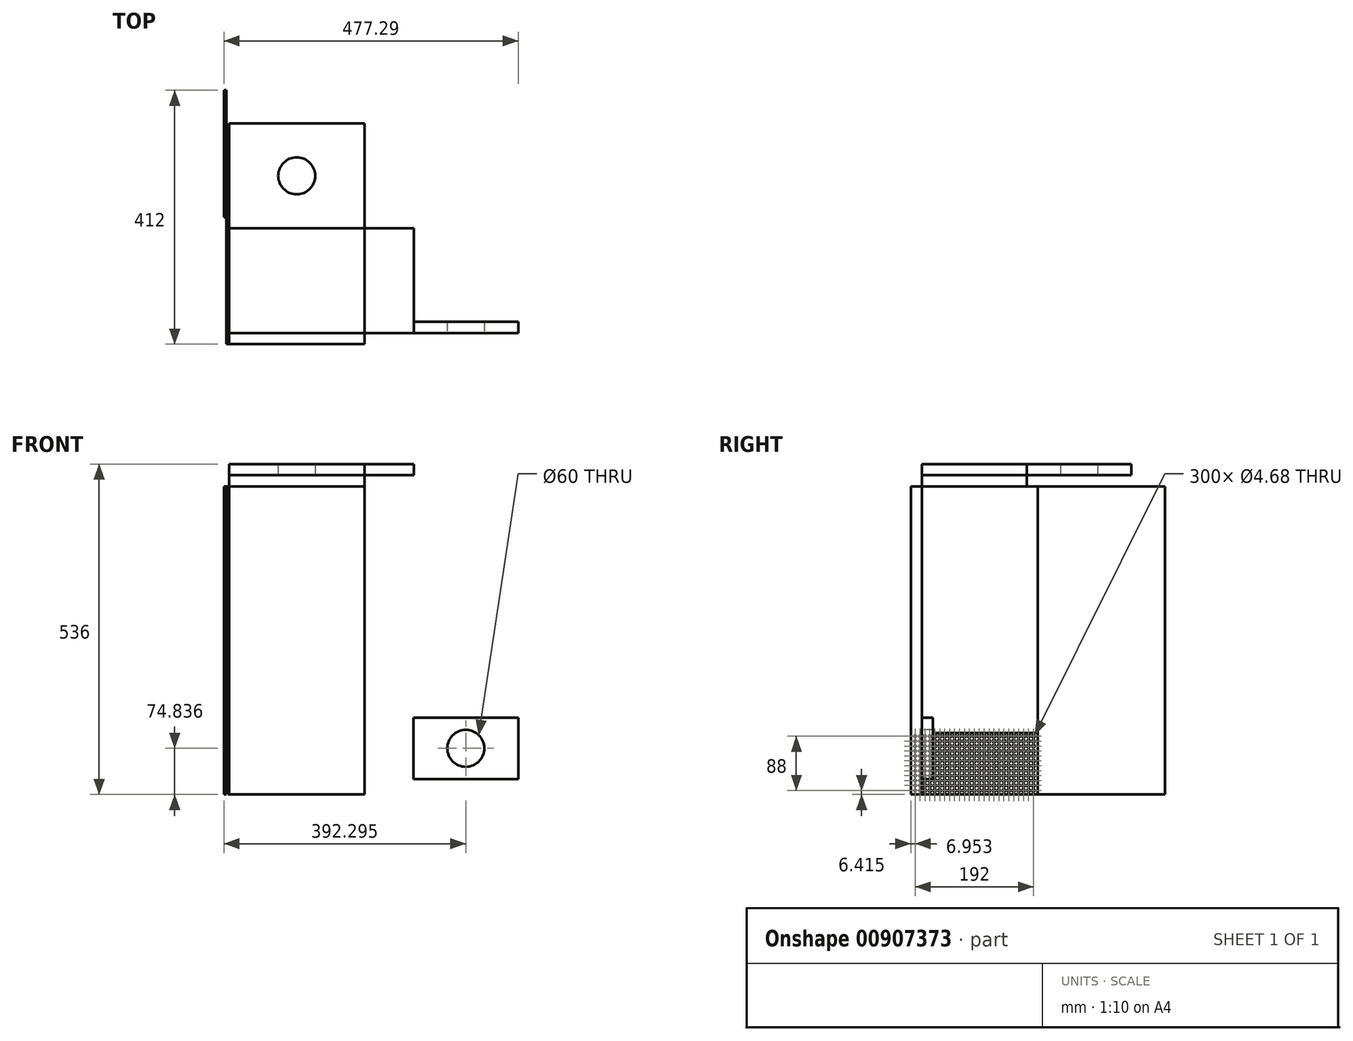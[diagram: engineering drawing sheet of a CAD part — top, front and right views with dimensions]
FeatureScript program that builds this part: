
annotation { "Feature Type Name" : "Feature", "Feature Type Description" : "" }
export const myFeature = defineFeature(function(context is Context, id is Id, definition is map)
    precondition{}
    {
        {
            var Q0;
            Q0=qCreatedBy(makeId("Front.planeOp"),FACE);
            var sketch = newSketch(context, id + "F0", { "sketchPlane" : qUnion([Q0])});
            skLineSegment(sketch, "E0.bottom", {"start": v(-107.52, 319.28) * mm, "end": v(112.48, 319.28) * mm});
            skLineSegment(sketch, "E0.top", {"start": v(-107.52, -180.72) * mm, "end": v(112.48, -180.72) * mm});
            skLineSegment(sketch, "E0.left", {"start": v(-107.52, 319.28) * mm, "end": v(-107.52, -180.72) * mm});
            skLineSegment(sketch, "E0.right", {"start": v(112.48, 319.28) * mm, "end": v(112.48, -180.72) * mm});
            skSolve(sketch);
        }
        {
            var Q0;
            Q0=makeQuery(id+"F0.imprint","IMPRINT",FACE,{"disambiguationData":[TD([[makeQuery(id+"F0.imprint","IMPRINT",EDGE,{"derivedFrom":sQuery(id+"F0.wireOp",EDGE,"E0.bottom")}),-1.0]])]});
            extrude(context, id + "F1", {"entities" : qUnion([Q0]), "depth" : 18 * mm, "offsetDistance" : 25 * mm});
        }
        {
            var Q0;
            Q0=makeQuery(id+"F1.opExtrude","SWEPT_FACE",FACE,{"disambiguationData":[OSD([sQuery(id+"F0.wireOp",EDGE,"E0.bottom")])]});
            var sketch = newSketch(context, id + "F2", { "sketchPlane" : qUnion([Q0])});
            skLineSegment(sketch, "E1.bottom", {"start": v(-107.52, 0) * mm, "end": v(112.48, 0) * mm});
            skLineSegment(sketch, "E1.top", {"start": v(-107.52, 170) * mm, "end": v(112.48, 170) * mm});
            skLineSegment(sketch, "E1.left", {"start": v(-107.52, 0) * mm, "end": v(-107.52, 170) * mm});
            skLineSegment(sketch, "E1.right", {"start": v(112.48, 0) * mm, "end": v(112.48, 170) * mm});
            skSolve(sketch);
        }
        {
            var Q0;
            Q0 = qSketchRegion(id + "F2", true);
            extrude(context, id + "F3", {"entities" : qUnion([Q0]), "depth" : 18 * mm, "offsetDistance" : 25 * mm});
        }
        {
            var Q0;
            Q0=makeQuery(id+"F3.opExtrude","CAP_FACE",FACE,{"disambiguationData":[OSD([sQuery(id+"F2.wireOp",EDGE,"E1.bottom"),sQuery(id+"F2.wireOp",EDGE,"E1.top"),sQuery(id+"F2.wireOp",EDGE,"E1.left"),sQuery(id+"F2.wireOp",EDGE,"E1.right")])],"isStart":false});
            var sketch = newSketch(context, id + "F4", { "sketchPlane" : qUnion([Q0])});
            skLineSegment(sketch, "E2.bottom", {"start": v(-107.52, 170) * mm, "end": v(112.48, 170) * mm});
            skLineSegment(sketch, "E2.top", {"start": v(-107.52, 340) * mm, "end": v(112.48, 340) * mm});
            skLineSegment(sketch, "E2.left", {"start": v(-107.52, 170) * mm, "end": v(-107.52, 340) * mm});
            skLineSegment(sketch, "E2.right", {"start": v(112.48, 170) * mm, "end": v(112.48, 340) * mm});
            skCircle(sketch, "E3", {"center": v(2.48, 255) * mm, "radius": 30 * mm});
            skPoint(sketch, "E3.centerSnap0", {"position": v(112.48, 255) * mm});
            skPoint(sketch, "E3.centerSnap1", {"position": v(2.48, 340) * mm});
            skSolve(sketch);
        }
        {
            var Q0;
            Q0 = qSketchRegion(id + "F4", true);
            extrude(context, id + "F5", {"entities" : qUnion([Q0]), "depth" : 18 * mm, "offsetDistance" : 25 * mm});
        }
        {
            var Q0;
            Q0=makeQuery(id+"F1.opExtrude","SWEPT_FACE",FACE,{"disambiguationData":[OSD([sQuery(id+"F0.wireOp",EDGE,"E0.left")])]});
            var sketch = newSketch(context, id + "F6", { "sketchPlane" : qUnion([Q0])});
            skLineSegment(sketch, "E4.bottom", {"start": v(18, 319.28) * mm, "end": v(-188, 319.28) * mm});
            skLineSegment(sketch, "E4.top", {"start": v(18, -80.72) * mm, "end": v(-188, -80.72) * mm});
            skLineSegment(sketch, "E4.left", {"start": v(18, 319.28) * mm, "end": v(18, -80.72) * mm});
            skLineSegment(sketch, "E4.right", {"start": v(-188, 319.28) * mm, "end": v(-188, -80.72) * mm});
            skSolve(sketch);
        }
        {
            var Q0;
            Q0 = qSketchRegion(id + "F6", true);
            extrude(context, id + "F7", {"entities" : qUnion([Q0]), "depth" : 4 * mm, "offsetDistance" : 25 * mm});
        }
        {
            var Q0;
            Q0=makeQuery(id+"F1.opExtrude","SWEPT_FACE",FACE,{"disambiguationData":[OSD([sQuery(id+"F0.wireOp",EDGE,"E0.left")])]});
            var sketch = newSketch(context, id + "F8", { "sketchPlane" : qUnion([Q0])});
            skLineSegment(sketch, "E5.bottom", {"start": v(18, -180.72) * mm, "end": v(-188, -180.72) * mm});
            skLineSegment(sketch, "E5.top", {"start": v(18, -80.72) * mm, "end": v(-188, -80.72) * mm});
            skLineSegment(sketch, "E5.left", {"start": v(18, -180.72) * mm, "end": v(18, -80.72) * mm});
            skLineSegment(sketch, "E5.right", {"start": v(-188, -180.72) * mm, "end": v(-188, -80.72) * mm});
            skCircle(sketch, "E6", {"center": v(-180.95, -86.3) * mm, "radius": 2.34 * mm});
            skCircle(sketch, "E7.0.1.0", {"center": v(-180.95, -94.3) * mm, "radius": 2.34 * mm});
            skCircle(sketch, "E7.0.2.0", {"center": v(-180.95, -102.3) * mm, "radius": 2.34 * mm});
            skCircle(sketch, "E7.0.3.0", {"center": v(-180.95, -110.3) * mm, "radius": 2.34 * mm});
            skCircle(sketch, "E7.0.4.0", {"center": v(-180.95, -118.3) * mm, "radius": 2.34 * mm});
            skCircle(sketch, "E7.0.5.0", {"center": v(-180.95, -126.3) * mm, "radius": 2.34 * mm});
            skCircle(sketch, "E7.0.6.0", {"center": v(-180.95, -134.3) * mm, "radius": 2.34 * mm});
            skCircle(sketch, "E7.0.7.0", {"center": v(-180.95, -142.3) * mm, "radius": 2.34 * mm});
            skCircle(sketch, "E7.0.8.0", {"center": v(-180.95, -150.3) * mm, "radius": 2.34 * mm});
            skCircle(sketch, "E7.0.9.0", {"center": v(-180.95, -158.3) * mm, "radius": 2.34 * mm});
            skCircle(sketch, "E7.0.10.0", {"center": v(-180.95, -166.3) * mm, "radius": 2.34 * mm});
            skCircle(sketch, "E7.0.11.0", {"center": v(-180.95, -174.3) * mm, "radius": 2.34 * mm});
            skCircle(sketch, "E7.1.0.0", {"center": v(-172.95, -86.3) * mm, "radius": 2.34 * mm});
            skCircle(sketch, "E7.1.1.0", {"center": v(-172.95, -94.3) * mm, "radius": 2.34 * mm});
            skCircle(sketch, "E7.1.2.0", {"center": v(-172.95, -102.3) * mm, "radius": 2.34 * mm});
            skCircle(sketch, "E7.1.3.0", {"center": v(-172.95, -110.3) * mm, "radius": 2.34 * mm});
            skCircle(sketch, "E7.1.4.0", {"center": v(-172.95, -118.3) * mm, "radius": 2.34 * mm});
            skCircle(sketch, "E7.1.5.0", {"center": v(-172.95, -126.3) * mm, "radius": 2.34 * mm});
            skCircle(sketch, "E7.1.6.0", {"center": v(-172.95, -134.3) * mm, "radius": 2.34 * mm});
            skCircle(sketch, "E7.1.7.0", {"center": v(-172.95, -142.3) * mm, "radius": 2.34 * mm});
            skCircle(sketch, "E7.1.8.0", {"center": v(-172.95, -150.3) * mm, "radius": 2.34 * mm});
            skCircle(sketch, "E7.1.9.0", {"center": v(-172.95, -158.3) * mm, "radius": 2.34 * mm});
            skCircle(sketch, "E7.1.10.0", {"center": v(-172.95, -166.3) * mm, "radius": 2.34 * mm});
            skCircle(sketch, "E7.1.11.0", {"center": v(-172.95, -174.3) * mm, "radius": 2.34 * mm});
            skCircle(sketch, "E7.2.0.0", {"center": v(-164.95, -86.3) * mm, "radius": 2.34 * mm});
            skCircle(sketch, "E7.2.1.0", {"center": v(-164.95, -94.3) * mm, "radius": 2.34 * mm});
            skCircle(sketch, "E7.2.2.0", {"center": v(-164.95, -102.3) * mm, "radius": 2.34 * mm});
            skCircle(sketch, "E7.2.3.0", {"center": v(-164.95, -110.3) * mm, "radius": 2.34 * mm});
            skCircle(sketch, "E7.2.4.0", {"center": v(-164.95, -118.3) * mm, "radius": 2.34 * mm});
            skCircle(sketch, "E7.2.5.0", {"center": v(-164.95, -126.3) * mm, "radius": 2.34 * mm});
            skCircle(sketch, "E7.2.6.0", {"center": v(-164.95, -134.3) * mm, "radius": 2.34 * mm});
            skCircle(sketch, "E7.2.7.0", {"center": v(-164.95, -142.3) * mm, "radius": 2.34 * mm});
            skCircle(sketch, "E7.2.8.0", {"center": v(-164.95, -150.3) * mm, "radius": 2.34 * mm});
            skCircle(sketch, "E7.2.9.0", {"center": v(-164.95, -158.3) * mm, "radius": 2.34 * mm});
            skCircle(sketch, "E7.2.10.0", {"center": v(-164.95, -166.3) * mm, "radius": 2.34 * mm});
            skCircle(sketch, "E7.2.11.0", {"center": v(-164.95, -174.3) * mm, "radius": 2.34 * mm});
            skCircle(sketch, "E7.3.0.0", {"center": v(-156.95, -86.3) * mm, "radius": 2.34 * mm});
            skCircle(sketch, "E7.3.1.0", {"center": v(-156.95, -94.3) * mm, "radius": 2.34 * mm});
            skCircle(sketch, "E7.3.2.0", {"center": v(-156.95, -102.3) * mm, "radius": 2.34 * mm});
            skCircle(sketch, "E7.3.3.0", {"center": v(-156.95, -110.3) * mm, "radius": 2.34 * mm});
            skCircle(sketch, "E7.3.4.0", {"center": v(-156.95, -118.3) * mm, "radius": 2.34 * mm});
            skCircle(sketch, "E7.3.5.0", {"center": v(-156.95, -126.3) * mm, "radius": 2.34 * mm});
            skCircle(sketch, "E7.3.6.0", {"center": v(-156.95, -134.3) * mm, "radius": 2.34 * mm});
            skCircle(sketch, "E7.3.7.0", {"center": v(-156.95, -142.3) * mm, "radius": 2.34 * mm});
            skCircle(sketch, "E7.3.8.0", {"center": v(-156.95, -150.3) * mm, "radius": 2.34 * mm});
            skCircle(sketch, "E7.3.9.0", {"center": v(-156.95, -158.3) * mm, "radius": 2.34 * mm});
            skCircle(sketch, "E7.3.10.0", {"center": v(-156.95, -166.3) * mm, "radius": 2.34 * mm});
            skCircle(sketch, "E7.3.11.0", {"center": v(-156.95, -174.3) * mm, "radius": 2.34 * mm});
            skCircle(sketch, "E7.4.0.0", {"center": v(-148.95, -86.3) * mm, "radius": 2.34 * mm});
            skCircle(sketch, "E7.4.1.0", {"center": v(-148.95, -94.3) * mm, "radius": 2.34 * mm});
            skCircle(sketch, "E7.4.2.0", {"center": v(-148.95, -102.3) * mm, "radius": 2.34 * mm});
            skCircle(sketch, "E7.4.3.0", {"center": v(-148.95, -110.3) * mm, "radius": 2.34 * mm});
            skCircle(sketch, "E7.4.4.0", {"center": v(-148.95, -118.3) * mm, "radius": 2.34 * mm});
            skCircle(sketch, "E7.4.5.0", {"center": v(-148.95, -126.3) * mm, "radius": 2.34 * mm});
            skCircle(sketch, "E7.4.6.0", {"center": v(-148.95, -134.3) * mm, "radius": 2.34 * mm});
            skCircle(sketch, "E7.4.7.0", {"center": v(-148.95, -142.3) * mm, "radius": 2.34 * mm});
            skCircle(sketch, "E7.4.8.0", {"center": v(-148.95, -150.3) * mm, "radius": 2.34 * mm});
            skCircle(sketch, "E7.4.9.0", {"center": v(-148.95, -158.3) * mm, "radius": 2.34 * mm});
            skCircle(sketch, "E7.4.10.0", {"center": v(-148.95, -166.3) * mm, "radius": 2.34 * mm});
            skCircle(sketch, "E7.4.11.0", {"center": v(-148.95, -174.3) * mm, "radius": 2.34 * mm});
            skCircle(sketch, "E7.5.0.0", {"center": v(-140.95, -86.3) * mm, "radius": 2.34 * mm});
            skCircle(sketch, "E7.5.1.0", {"center": v(-140.95, -94.3) * mm, "radius": 2.34 * mm});
            skCircle(sketch, "E7.5.2.0", {"center": v(-140.95, -102.3) * mm, "radius": 2.34 * mm});
            skCircle(sketch, "E7.5.3.0", {"center": v(-140.95, -110.3) * mm, "radius": 2.34 * mm});
            skCircle(sketch, "E7.5.4.0", {"center": v(-140.95, -118.3) * mm, "radius": 2.34 * mm});
            skCircle(sketch, "E7.5.5.0", {"center": v(-140.95, -126.3) * mm, "radius": 2.34 * mm});
            skCircle(sketch, "E7.5.6.0", {"center": v(-140.95, -134.3) * mm, "radius": 2.34 * mm});
            skCircle(sketch, "E7.5.7.0", {"center": v(-140.95, -142.3) * mm, "radius": 2.34 * mm});
            skCircle(sketch, "E7.5.8.0", {"center": v(-140.95, -150.3) * mm, "radius": 2.34 * mm});
            skCircle(sketch, "E7.5.9.0", {"center": v(-140.95, -158.3) * mm, "radius": 2.34 * mm});
            skCircle(sketch, "E7.5.10.0", {"center": v(-140.95, -166.3) * mm, "radius": 2.34 * mm});
            skCircle(sketch, "E7.5.11.0", {"center": v(-140.95, -174.3) * mm, "radius": 2.34 * mm});
            skCircle(sketch, "E7.6.0.0", {"center": v(-132.95, -86.3) * mm, "radius": 2.34 * mm});
            skCircle(sketch, "E7.6.1.0", {"center": v(-132.95, -94.3) * mm, "radius": 2.34 * mm});
            skCircle(sketch, "E7.6.2.0", {"center": v(-132.95, -102.3) * mm, "radius": 2.34 * mm});
            skCircle(sketch, "E7.6.3.0", {"center": v(-132.95, -110.3) * mm, "radius": 2.34 * mm});
            skCircle(sketch, "E7.6.4.0", {"center": v(-132.95, -118.3) * mm, "radius": 2.34 * mm});
            skCircle(sketch, "E7.6.5.0", {"center": v(-132.95, -126.3) * mm, "radius": 2.34 * mm});
            skCircle(sketch, "E7.6.6.0", {"center": v(-132.95, -134.3) * mm, "radius": 2.34 * mm});
            skCircle(sketch, "E7.6.7.0", {"center": v(-132.95, -142.3) * mm, "radius": 2.34 * mm});
            skCircle(sketch, "E7.6.8.0", {"center": v(-132.95, -150.3) * mm, "radius": 2.34 * mm});
            skCircle(sketch, "E7.6.9.0", {"center": v(-132.95, -158.3) * mm, "radius": 2.34 * mm});
            skCircle(sketch, "E7.6.10.0", {"center": v(-132.95, -166.3) * mm, "radius": 2.34 * mm});
            skCircle(sketch, "E7.6.11.0", {"center": v(-132.95, -174.3) * mm, "radius": 2.34 * mm});
            skCircle(sketch, "E7.7.0.0", {"center": v(-124.95, -86.3) * mm, "radius": 2.34 * mm});
            skCircle(sketch, "E7.7.1.0", {"center": v(-124.95, -94.3) * mm, "radius": 2.34 * mm});
            skCircle(sketch, "E7.7.2.0", {"center": v(-124.95, -102.3) * mm, "radius": 2.34 * mm});
            skCircle(sketch, "E7.7.3.0", {"center": v(-124.95, -110.3) * mm, "radius": 2.34 * mm});
            skCircle(sketch, "E7.7.4.0", {"center": v(-124.95, -118.3) * mm, "radius": 2.34 * mm});
            skCircle(sketch, "E7.7.5.0", {"center": v(-124.95, -126.3) * mm, "radius": 2.34 * mm});
            skCircle(sketch, "E7.7.6.0", {"center": v(-124.95, -134.3) * mm, "radius": 2.34 * mm});
            skCircle(sketch, "E7.7.7.0", {"center": v(-124.95, -142.3) * mm, "radius": 2.34 * mm});
            skCircle(sketch, "E7.7.8.0", {"center": v(-124.95, -150.3) * mm, "radius": 2.34 * mm});
            skCircle(sketch, "E7.7.9.0", {"center": v(-124.95, -158.3) * mm, "radius": 2.34 * mm});
            skCircle(sketch, "E7.7.10.0", {"center": v(-124.95, -166.3) * mm, "radius": 2.34 * mm});
            skCircle(sketch, "E7.7.11.0", {"center": v(-124.95, -174.3) * mm, "radius": 2.34 * mm});
            skCircle(sketch, "E7.8.0.0", {"center": v(-116.95, -86.3) * mm, "radius": 2.34 * mm});
            skCircle(sketch, "E7.8.1.0", {"center": v(-116.95, -94.3) * mm, "radius": 2.34 * mm});
            skCircle(sketch, "E7.8.2.0", {"center": v(-116.95, -102.3) * mm, "radius": 2.34 * mm});
            skCircle(sketch, "E7.8.3.0", {"center": v(-116.95, -110.3) * mm, "radius": 2.34 * mm});
            skCircle(sketch, "E7.8.4.0", {"center": v(-116.95, -118.3) * mm, "radius": 2.34 * mm});
            skCircle(sketch, "E7.8.5.0", {"center": v(-116.95, -126.3) * mm, "radius": 2.34 * mm});
            skCircle(sketch, "E7.8.6.0", {"center": v(-116.95, -134.3) * mm, "radius": 2.34 * mm});
            skCircle(sketch, "E7.8.7.0", {"center": v(-116.95, -142.3) * mm, "radius": 2.34 * mm});
            skCircle(sketch, "E7.8.8.0", {"center": v(-116.95, -150.3) * mm, "radius": 2.34 * mm});
            skCircle(sketch, "E7.8.9.0", {"center": v(-116.95, -158.3) * mm, "radius": 2.34 * mm});
            skCircle(sketch, "E7.8.10.0", {"center": v(-116.95, -166.3) * mm, "radius": 2.34 * mm});
            skCircle(sketch, "E7.8.11.0", {"center": v(-116.95, -174.3) * mm, "radius": 2.34 * mm});
            skCircle(sketch, "E7.9.0.0", {"center": v(-108.95, -86.3) * mm, "radius": 2.34 * mm});
            skCircle(sketch, "E7.9.1.0", {"center": v(-108.95, -94.3) * mm, "radius": 2.34 * mm});
            skCircle(sketch, "E7.9.2.0", {"center": v(-108.95, -102.3) * mm, "radius": 2.34 * mm});
            skCircle(sketch, "E7.9.3.0", {"center": v(-108.95, -110.3) * mm, "radius": 2.34 * mm});
            skCircle(sketch, "E7.9.4.0", {"center": v(-108.95, -118.3) * mm, "radius": 2.34 * mm});
            skCircle(sketch, "E7.9.5.0", {"center": v(-108.95, -126.3) * mm, "radius": 2.34 * mm});
            skCircle(sketch, "E7.9.6.0", {"center": v(-108.95, -134.3) * mm, "radius": 2.34 * mm});
            skCircle(sketch, "E7.9.7.0", {"center": v(-108.95, -142.3) * mm, "radius": 2.34 * mm});
            skCircle(sketch, "E7.9.8.0", {"center": v(-108.95, -150.3) * mm, "radius": 2.34 * mm});
            skCircle(sketch, "E7.9.9.0", {"center": v(-108.95, -158.3) * mm, "radius": 2.34 * mm});
            skCircle(sketch, "E7.9.10.0", {"center": v(-108.95, -166.3) * mm, "radius": 2.34 * mm});
            skCircle(sketch, "E7.9.11.0", {"center": v(-108.95, -174.3) * mm, "radius": 2.34 * mm});
            skCircle(sketch, "E7.10.0.0", {"center": v(-100.95, -86.3) * mm, "radius": 2.34 * mm});
            skCircle(sketch, "E7.10.1.0", {"center": v(-100.95, -94.3) * mm, "radius": 2.34 * mm});
            skCircle(sketch, "E7.10.2.0", {"center": v(-100.95, -102.3) * mm, "radius": 2.34 * mm});
            skCircle(sketch, "E7.10.3.0", {"center": v(-100.95, -110.3) * mm, "radius": 2.34 * mm});
            skCircle(sketch, "E7.10.4.0", {"center": v(-100.95, -118.3) * mm, "radius": 2.34 * mm});
            skCircle(sketch, "E7.10.5.0", {"center": v(-100.95, -126.3) * mm, "radius": 2.34 * mm});
            skCircle(sketch, "E7.10.6.0", {"center": v(-100.95, -134.3) * mm, "radius": 2.34 * mm});
            skCircle(sketch, "E7.10.7.0", {"center": v(-100.95, -142.3) * mm, "radius": 2.34 * mm});
            skCircle(sketch, "E7.10.8.0", {"center": v(-100.95, -150.3) * mm, "radius": 2.34 * mm});
            skCircle(sketch, "E7.10.9.0", {"center": v(-100.95, -158.3) * mm, "radius": 2.34 * mm});
            skCircle(sketch, "E7.10.10.0", {"center": v(-100.95, -166.3) * mm, "radius": 2.34 * mm});
            skCircle(sketch, "E7.10.11.0", {"center": v(-100.95, -174.3) * mm, "radius": 2.34 * mm});
            skCircle(sketch, "E7.11.0.0", {"center": v(-92.95, -86.3) * mm, "radius": 2.34 * mm});
            skCircle(sketch, "E7.11.1.0", {"center": v(-92.95, -94.3) * mm, "radius": 2.34 * mm});
            skCircle(sketch, "E7.11.2.0", {"center": v(-92.95, -102.3) * mm, "radius": 2.34 * mm});
            skCircle(sketch, "E7.11.3.0", {"center": v(-92.95, -110.3) * mm, "radius": 2.34 * mm});
            skCircle(sketch, "E7.11.4.0", {"center": v(-92.95, -118.3) * mm, "radius": 2.34 * mm});
            skCircle(sketch, "E7.11.5.0", {"center": v(-92.95, -126.3) * mm, "radius": 2.34 * mm});
            skCircle(sketch, "E7.11.6.0", {"center": v(-92.95, -134.3) * mm, "radius": 2.34 * mm});
            skCircle(sketch, "E7.11.7.0", {"center": v(-92.95, -142.3) * mm, "radius": 2.34 * mm});
            skCircle(sketch, "E7.11.8.0", {"center": v(-92.95, -150.3) * mm, "radius": 2.34 * mm});
            skCircle(sketch, "E7.11.9.0", {"center": v(-92.95, -158.3) * mm, "radius": 2.34 * mm});
            skCircle(sketch, "E7.11.10.0", {"center": v(-92.95, -166.3) * mm, "radius": 2.34 * mm});
            skCircle(sketch, "E7.11.11.0", {"center": v(-92.95, -174.3) * mm, "radius": 2.34 * mm});
            skCircle(sketch, "E7.12.0.0", {"center": v(-84.95, -86.3) * mm, "radius": 2.34 * mm});
            skCircle(sketch, "E7.12.1.0", {"center": v(-84.95, -94.3) * mm, "radius": 2.34 * mm});
            skCircle(sketch, "E7.12.2.0", {"center": v(-84.95, -102.3) * mm, "radius": 2.34 * mm});
            skCircle(sketch, "E7.12.3.0", {"center": v(-84.95, -110.3) * mm, "radius": 2.34 * mm});
            skCircle(sketch, "E7.12.4.0", {"center": v(-84.95, -118.3) * mm, "radius": 2.34 * mm});
            skCircle(sketch, "E7.12.5.0", {"center": v(-84.95, -126.3) * mm, "radius": 2.34 * mm});
            skCircle(sketch, "E7.12.6.0", {"center": v(-84.95, -134.3) * mm, "radius": 2.34 * mm});
            skCircle(sketch, "E7.12.7.0", {"center": v(-84.95, -142.3) * mm, "radius": 2.34 * mm});
            skCircle(sketch, "E7.12.8.0", {"center": v(-84.95, -150.3) * mm, "radius": 2.34 * mm});
            skCircle(sketch, "E7.12.9.0", {"center": v(-84.95, -158.3) * mm, "radius": 2.34 * mm});
            skCircle(sketch, "E7.12.10.0", {"center": v(-84.95, -166.3) * mm, "radius": 2.34 * mm});
            skCircle(sketch, "E7.12.11.0", {"center": v(-84.95, -174.3) * mm, "radius": 2.34 * mm});
            skCircle(sketch, "E7.13.0.0", {"center": v(-76.95, -86.3) * mm, "radius": 2.34 * mm});
            skCircle(sketch, "E7.13.1.0", {"center": v(-76.95, -94.3) * mm, "radius": 2.34 * mm});
            skCircle(sketch, "E7.13.2.0", {"center": v(-76.95, -102.3) * mm, "radius": 2.34 * mm});
            skCircle(sketch, "E7.13.3.0", {"center": v(-76.95, -110.3) * mm, "radius": 2.34 * mm});
            skCircle(sketch, "E7.13.4.0", {"center": v(-76.95, -118.3) * mm, "radius": 2.34 * mm});
            skCircle(sketch, "E7.13.5.0", {"center": v(-76.95, -126.3) * mm, "radius": 2.34 * mm});
            skCircle(sketch, "E7.13.6.0", {"center": v(-76.95, -134.3) * mm, "radius": 2.34 * mm});
            skCircle(sketch, "E7.13.7.0", {"center": v(-76.95, -142.3) * mm, "radius": 2.34 * mm});
            skCircle(sketch, "E7.13.8.0", {"center": v(-76.95, -150.3) * mm, "radius": 2.34 * mm});
            skCircle(sketch, "E7.13.9.0", {"center": v(-76.95, -158.3) * mm, "radius": 2.34 * mm});
            skCircle(sketch, "E7.13.10.0", {"center": v(-76.95, -166.3) * mm, "radius": 2.34 * mm});
            skCircle(sketch, "E7.13.11.0", {"center": v(-76.95, -174.3) * mm, "radius": 2.34 * mm});
            skCircle(sketch, "E7.14.0.0", {"center": v(-68.95, -86.3) * mm, "radius": 2.34 * mm});
            skCircle(sketch, "E7.14.1.0", {"center": v(-68.95, -94.3) * mm, "radius": 2.34 * mm});
            skCircle(sketch, "E7.14.2.0", {"center": v(-68.95, -102.3) * mm, "radius": 2.34 * mm});
            skCircle(sketch, "E7.14.3.0", {"center": v(-68.95, -110.3) * mm, "radius": 2.34 * mm});
            skCircle(sketch, "E7.14.4.0", {"center": v(-68.95, -118.3) * mm, "radius": 2.34 * mm});
            skCircle(sketch, "E7.14.5.0", {"center": v(-68.95, -126.3) * mm, "radius": 2.34 * mm});
            skCircle(sketch, "E7.14.6.0", {"center": v(-68.95, -134.3) * mm, "radius": 2.34 * mm});
            skCircle(sketch, "E7.14.7.0", {"center": v(-68.95, -142.3) * mm, "radius": 2.34 * mm});
            skCircle(sketch, "E7.14.8.0", {"center": v(-68.95, -150.3) * mm, "radius": 2.34 * mm});
            skCircle(sketch, "E7.14.9.0", {"center": v(-68.95, -158.3) * mm, "radius": 2.34 * mm});
            skCircle(sketch, "E7.14.10.0", {"center": v(-68.95, -166.3) * mm, "radius": 2.34 * mm});
            skCircle(sketch, "E7.14.11.0", {"center": v(-68.95, -174.3) * mm, "radius": 2.34 * mm});
            skCircle(sketch, "E7.15.0.0", {"center": v(-60.95, -86.3) * mm, "radius": 2.34 * mm});
            skCircle(sketch, "E7.15.1.0", {"center": v(-60.95, -94.3) * mm, "radius": 2.34 * mm});
            skCircle(sketch, "E7.15.2.0", {"center": v(-60.95, -102.3) * mm, "radius": 2.34 * mm});
            skCircle(sketch, "E7.15.3.0", {"center": v(-60.95, -110.3) * mm, "radius": 2.34 * mm});
            skCircle(sketch, "E7.15.4.0", {"center": v(-60.95, -118.3) * mm, "radius": 2.34 * mm});
            skCircle(sketch, "E7.15.5.0", {"center": v(-60.95, -126.3) * mm, "radius": 2.34 * mm});
            skCircle(sketch, "E7.15.6.0", {"center": v(-60.95, -134.3) * mm, "radius": 2.34 * mm});
            skCircle(sketch, "E7.15.7.0", {"center": v(-60.95, -142.3) * mm, "radius": 2.34 * mm});
            skCircle(sketch, "E7.15.8.0", {"center": v(-60.95, -150.3) * mm, "radius": 2.34 * mm});
            skCircle(sketch, "E7.15.9.0", {"center": v(-60.95, -158.3) * mm, "radius": 2.34 * mm});
            skCircle(sketch, "E7.15.10.0", {"center": v(-60.95, -166.3) * mm, "radius": 2.34 * mm});
            skCircle(sketch, "E7.15.11.0", {"center": v(-60.95, -174.3) * mm, "radius": 2.34 * mm});
            skCircle(sketch, "E7.16.0.0", {"center": v(-52.95, -86.3) * mm, "radius": 2.34 * mm});
            skCircle(sketch, "E7.16.1.0", {"center": v(-52.95, -94.3) * mm, "radius": 2.34 * mm});
            skCircle(sketch, "E7.16.2.0", {"center": v(-52.95, -102.3) * mm, "radius": 2.34 * mm});
            skCircle(sketch, "E7.16.3.0", {"center": v(-52.95, -110.3) * mm, "radius": 2.34 * mm});
            skCircle(sketch, "E7.16.4.0", {"center": v(-52.95, -118.3) * mm, "radius": 2.34 * mm});
            skCircle(sketch, "E7.16.5.0", {"center": v(-52.95, -126.3) * mm, "radius": 2.34 * mm});
            skCircle(sketch, "E7.16.6.0", {"center": v(-52.95, -134.3) * mm, "radius": 2.34 * mm});
            skCircle(sketch, "E7.16.7.0", {"center": v(-52.95, -142.3) * mm, "radius": 2.34 * mm});
            skCircle(sketch, "E7.16.8.0", {"center": v(-52.95, -150.3) * mm, "radius": 2.34 * mm});
            skCircle(sketch, "E7.16.9.0", {"center": v(-52.95, -158.3) * mm, "radius": 2.34 * mm});
            skCircle(sketch, "E7.16.10.0", {"center": v(-52.95, -166.3) * mm, "radius": 2.34 * mm});
            skCircle(sketch, "E7.16.11.0", {"center": v(-52.95, -174.3) * mm, "radius": 2.34 * mm});
            skCircle(sketch, "E7.17.0.0", {"center": v(-44.95, -86.3) * mm, "radius": 2.34 * mm});
            skCircle(sketch, "E7.17.1.0", {"center": v(-44.95, -94.3) * mm, "radius": 2.34 * mm});
            skCircle(sketch, "E7.17.2.0", {"center": v(-44.95, -102.3) * mm, "radius": 2.34 * mm});
            skCircle(sketch, "E7.17.3.0", {"center": v(-44.95, -110.3) * mm, "radius": 2.34 * mm});
            skCircle(sketch, "E7.17.4.0", {"center": v(-44.95, -118.3) * mm, "radius": 2.34 * mm});
            skCircle(sketch, "E7.17.5.0", {"center": v(-44.95, -126.3) * mm, "radius": 2.34 * mm});
            skCircle(sketch, "E7.17.6.0", {"center": v(-44.95, -134.3) * mm, "radius": 2.34 * mm});
            skCircle(sketch, "E7.17.7.0", {"center": v(-44.95, -142.3) * mm, "radius": 2.34 * mm});
            skCircle(sketch, "E7.17.8.0", {"center": v(-44.95, -150.3) * mm, "radius": 2.34 * mm});
            skCircle(sketch, "E7.17.9.0", {"center": v(-44.95, -158.3) * mm, "radius": 2.34 * mm});
            skCircle(sketch, "E7.17.10.0", {"center": v(-44.95, -166.3) * mm, "radius": 2.34 * mm});
            skCircle(sketch, "E7.17.11.0", {"center": v(-44.95, -174.3) * mm, "radius": 2.34 * mm});
            skCircle(sketch, "E7.18.0.0", {"center": v(-36.95, -86.3) * mm, "radius": 2.34 * mm});
            skCircle(sketch, "E7.18.1.0", {"center": v(-36.95, -94.3) * mm, "radius": 2.34 * mm});
            skCircle(sketch, "E7.18.2.0", {"center": v(-36.95, -102.3) * mm, "radius": 2.34 * mm});
            skCircle(sketch, "E7.18.3.0", {"center": v(-36.95, -110.3) * mm, "radius": 2.34 * mm});
            skCircle(sketch, "E7.18.4.0", {"center": v(-36.95, -118.3) * mm, "radius": 2.34 * mm});
            skCircle(sketch, "E7.18.5.0", {"center": v(-36.95, -126.3) * mm, "radius": 2.34 * mm});
            skCircle(sketch, "E7.18.6.0", {"center": v(-36.95, -134.3) * mm, "radius": 2.34 * mm});
            skCircle(sketch, "E7.18.7.0", {"center": v(-36.95, -142.3) * mm, "radius": 2.34 * mm});
            skCircle(sketch, "E7.18.8.0", {"center": v(-36.95, -150.3) * mm, "radius": 2.34 * mm});
            skCircle(sketch, "E7.18.9.0", {"center": v(-36.95, -158.3) * mm, "radius": 2.34 * mm});
            skCircle(sketch, "E7.18.10.0", {"center": v(-36.95, -166.3) * mm, "radius": 2.34 * mm});
            skCircle(sketch, "E7.18.11.0", {"center": v(-36.95, -174.3) * mm, "radius": 2.34 * mm});
            skCircle(sketch, "E7.19.0.0", {"center": v(-28.95, -86.3) * mm, "radius": 2.34 * mm});
            skCircle(sketch, "E7.19.1.0", {"center": v(-28.95, -94.3) * mm, "radius": 2.34 * mm});
            skCircle(sketch, "E7.19.2.0", {"center": v(-28.95, -102.3) * mm, "radius": 2.34 * mm});
            skCircle(sketch, "E7.19.3.0", {"center": v(-28.95, -110.3) * mm, "radius": 2.34 * mm});
            skCircle(sketch, "E7.19.4.0", {"center": v(-28.95, -118.3) * mm, "radius": 2.34 * mm});
            skCircle(sketch, "E7.19.5.0", {"center": v(-28.95, -126.3) * mm, "radius": 2.34 * mm});
            skCircle(sketch, "E7.19.6.0", {"center": v(-28.95, -134.3) * mm, "radius": 2.34 * mm});
            skCircle(sketch, "E7.19.7.0", {"center": v(-28.95, -142.3) * mm, "radius": 2.34 * mm});
            skCircle(sketch, "E7.19.8.0", {"center": v(-28.95, -150.3) * mm, "radius": 2.34 * mm});
            skCircle(sketch, "E7.19.9.0", {"center": v(-28.95, -158.3) * mm, "radius": 2.34 * mm});
            skCircle(sketch, "E7.19.10.0", {"center": v(-28.95, -166.3) * mm, "radius": 2.34 * mm});
            skCircle(sketch, "E7.19.11.0", {"center": v(-28.95, -174.3) * mm, "radius": 2.34 * mm});
            skCircle(sketch, "E7.20.0.0", {"center": v(-20.95, -86.3) * mm, "radius": 2.34 * mm});
            skCircle(sketch, "E7.20.1.0", {"center": v(-20.95, -94.3) * mm, "radius": 2.34 * mm});
            skCircle(sketch, "E7.20.2.0", {"center": v(-20.95, -102.3) * mm, "radius": 2.34 * mm});
            skCircle(sketch, "E7.20.3.0", {"center": v(-20.95, -110.3) * mm, "radius": 2.34 * mm});
            skCircle(sketch, "E7.20.4.0", {"center": v(-20.95, -118.3) * mm, "radius": 2.34 * mm});
            skCircle(sketch, "E7.20.5.0", {"center": v(-20.95, -126.3) * mm, "radius": 2.34 * mm});
            skCircle(sketch, "E7.20.6.0", {"center": v(-20.95, -134.3) * mm, "radius": 2.34 * mm});
            skCircle(sketch, "E7.20.7.0", {"center": v(-20.95, -142.3) * mm, "radius": 2.34 * mm});
            skCircle(sketch, "E7.20.8.0", {"center": v(-20.95, -150.3) * mm, "radius": 2.34 * mm});
            skCircle(sketch, "E7.20.9.0", {"center": v(-20.95, -158.3) * mm, "radius": 2.34 * mm});
            skCircle(sketch, "E7.20.10.0", {"center": v(-20.95, -166.3) * mm, "radius": 2.34 * mm});
            skCircle(sketch, "E7.20.11.0", {"center": v(-20.95, -174.3) * mm, "radius": 2.34 * mm});
            skCircle(sketch, "E7.21.0.0", {"center": v(-12.95, -86.3) * mm, "radius": 2.34 * mm});
            skCircle(sketch, "E7.21.1.0", {"center": v(-12.95, -94.3) * mm, "radius": 2.34 * mm});
            skCircle(sketch, "E7.21.2.0", {"center": v(-12.95, -102.3) * mm, "radius": 2.34 * mm});
            skCircle(sketch, "E7.21.3.0", {"center": v(-12.95, -110.3) * mm, "radius": 2.34 * mm});
            skCircle(sketch, "E7.21.4.0", {"center": v(-12.95, -118.3) * mm, "radius": 2.34 * mm});
            skCircle(sketch, "E7.21.5.0", {"center": v(-12.95, -126.3) * mm, "radius": 2.34 * mm});
            skCircle(sketch, "E7.21.6.0", {"center": v(-12.95, -134.3) * mm, "radius": 2.34 * mm});
            skCircle(sketch, "E7.21.7.0", {"center": v(-12.95, -142.3) * mm, "radius": 2.34 * mm});
            skCircle(sketch, "E7.21.8.0", {"center": v(-12.95, -150.3) * mm, "radius": 2.34 * mm});
            skCircle(sketch, "E7.21.9.0", {"center": v(-12.95, -158.3) * mm, "radius": 2.34 * mm});
            skCircle(sketch, "E7.21.10.0", {"center": v(-12.95, -166.3) * mm, "radius": 2.34 * mm});
            skCircle(sketch, "E7.21.11.0", {"center": v(-12.95, -174.3) * mm, "radius": 2.34 * mm});
            skCircle(sketch, "E7.22.0.0", {"center": v(-4.95, -86.3) * mm, "radius": 2.34 * mm});
            skCircle(sketch, "E7.22.1.0", {"center": v(-4.95, -94.3) * mm, "radius": 2.34 * mm});
            skCircle(sketch, "E7.22.2.0", {"center": v(-4.95, -102.3) * mm, "radius": 2.34 * mm});
            skCircle(sketch, "E7.22.3.0", {"center": v(-4.95, -110.3) * mm, "radius": 2.34 * mm});
            skCircle(sketch, "E7.22.4.0", {"center": v(-4.95, -118.3) * mm, "radius": 2.34 * mm});
            skCircle(sketch, "E7.22.5.0", {"center": v(-4.95, -126.3) * mm, "radius": 2.34 * mm});
            skCircle(sketch, "E7.22.6.0", {"center": v(-4.95, -134.3) * mm, "radius": 2.34 * mm});
            skCircle(sketch, "E7.22.7.0", {"center": v(-4.95, -142.3) * mm, "radius": 2.34 * mm});
            skCircle(sketch, "E7.22.8.0", {"center": v(-4.95, -150.3) * mm, "radius": 2.34 * mm});
            skCircle(sketch, "E7.22.9.0", {"center": v(-4.95, -158.3) * mm, "radius": 2.34 * mm});
            skCircle(sketch, "E7.22.10.0", {"center": v(-4.95, -166.3) * mm, "radius": 2.34 * mm});
            skCircle(sketch, "E7.22.11.0", {"center": v(-4.95, -174.3) * mm, "radius": 2.34 * mm});
            skLineSegment(sketch, "E7.direction1", {"start": v(-180.95, -86.3) * mm, "end": v(-172.95, -86.3) * mm, "construction": true});
            skLineSegment(sketch, "E7.direction2", {"start": v(-180.95, -86.3) * mm, "end": v(-180.95, -94.3) * mm, "construction": true});
            skCircle(sketch, "E8.0.23.0", {"center": v(3.05, -86.3) * mm, "radius": 2.34 * mm});
            skCircle(sketch, "E8.0.23.1", {"center": v(3.05, -94.3) * mm, "radius": 2.34 * mm});
            skCircle(sketch, "E8.0.23.2", {"center": v(3.05, -102.3) * mm, "radius": 2.34 * mm});
            skCircle(sketch, "E8.0.23.3", {"center": v(3.05, -110.3) * mm, "radius": 2.34 * mm});
            skCircle(sketch, "E8.0.23.4", {"center": v(3.05, -118.3) * mm, "radius": 2.34 * mm});
            skCircle(sketch, "E8.0.23.5", {"center": v(3.05, -126.3) * mm, "radius": 2.34 * mm});
            skCircle(sketch, "E8.0.23.6", {"center": v(3.05, -134.3) * mm, "radius": 2.34 * mm});
            skCircle(sketch, "E8.0.23.7", {"center": v(3.05, -142.3) * mm, "radius": 2.34 * mm});
            skCircle(sketch, "E8.0.23.8", {"center": v(3.05, -150.3) * mm, "radius": 2.34 * mm});
            skCircle(sketch, "E8.0.23.9", {"center": v(3.05, -158.3) * mm, "radius": 2.34 * mm});
            skCircle(sketch, "E8.0.23.10", {"center": v(3.05, -166.3) * mm, "radius": 2.34 * mm});
            skCircle(sketch, "E8.0.23.11", {"center": v(3.05, -174.3) * mm, "radius": 2.34 * mm});
            skCircle(sketch, "E8.0.24.0", {"center": v(11.05, -86.3) * mm, "radius": 2.34 * mm});
            skCircle(sketch, "E8.0.24.1", {"center": v(11.05, -94.3) * mm, "radius": 2.34 * mm});
            skCircle(sketch, "E8.0.24.2", {"center": v(11.05, -102.3) * mm, "radius": 2.34 * mm});
            skCircle(sketch, "E8.0.24.3", {"center": v(11.05, -110.3) * mm, "radius": 2.34 * mm});
            skCircle(sketch, "E8.0.24.4", {"center": v(11.05, -118.3) * mm, "radius": 2.34 * mm});
            skCircle(sketch, "E8.0.24.5", {"center": v(11.05, -126.3) * mm, "radius": 2.34 * mm});
            skCircle(sketch, "E8.0.24.6", {"center": v(11.05, -134.3) * mm, "radius": 2.34 * mm});
            skCircle(sketch, "E8.0.24.7", {"center": v(11.05, -142.3) * mm, "radius": 2.34 * mm});
            skCircle(sketch, "E8.0.24.8", {"center": v(11.05, -150.3) * mm, "radius": 2.34 * mm});
            skCircle(sketch, "E8.0.24.9", {"center": v(11.05, -158.3) * mm, "radius": 2.34 * mm});
            skCircle(sketch, "E8.0.24.10", {"center": v(11.05, -166.3) * mm, "radius": 2.34 * mm});
            skCircle(sketch, "E8.0.24.11", {"center": v(11.05, -174.3) * mm, "radius": 2.34 * mm});
            skSolve(sketch);
        }
        {
            var Q0;
            Q0 = qSketchRegion(id + "F8", true);
            extrude(context, id + "F9", {"entities" : qUnion([Q0]), "depth" : 1.5 * mm, "offsetDistance" : 25 * mm});
        }
        {
            var Q0;
            Q0=makeQuery(id+"F1.opExtrude","CAP_FACE",FACE,{"disambiguationData":[OSD([sQuery(id+"F0.wireOp",EDGE,"E0.bottom"),sQuery(id+"F0.wireOp",EDGE,"E0.top"),sQuery(id+"F0.wireOp",EDGE,"E0.left"),sQuery(id+"F0.wireOp",EDGE,"E0.right")])],"isStart":true});
            var sketch = newSketch(context, id + "F10", { "sketchPlane" : qUnion([Q0])});
            skLineSegment(sketch, "E9.bottom", {"start": v(-191.77, -155.88) * mm, "end": v(-361.77, -155.88) * mm});
            skLineSegment(sketch, "E9.top", {"start": v(-191.77, -55.88) * mm, "end": v(-361.77, -55.88) * mm});
            skLineSegment(sketch, "E9.left", {"start": v(-191.77, -155.88) * mm, "end": v(-191.77, -55.88) * mm});
            skLineSegment(sketch, "E9.right", {"start": v(-361.77, -155.88) * mm, "end": v(-361.77, -55.88) * mm});
            skCircle(sketch, "E10", {"center": v(-276.77, -105.88) * mm, "radius": 30 * mm});
            skPoint(sketch, "E10.centerSnap0", {"position": v(-191.77, -105.88) * mm});
            skPoint(sketch, "E10.centerSnap1", {"position": v(-276.77, -55.88) * mm});
            skSolve(sketch);
        }
        {
            var Q0;
            Q0 = qSketchRegion(id + "F10", true);
            extrude(context, id + "F11", {"entities" : qUnion([Q0]), "depth" : 18 * mm, "offsetDistance" : 25 * mm});
        }
        {
            var Q0;
            Q0=makeQuery(id+"F7.opExtrude","CAP_FACE",FACE,{"disambiguationData":[OSD([sQuery(id+"F6.wireOp",EDGE,"E4.bottom"),sQuery(id+"F6.wireOp",EDGE,"E4.top"),sQuery(id+"F6.wireOp",EDGE,"E4.left"),sQuery(id+"F6.wireOp",EDGE,"E4.right")])],"isStart":false});
            var sketch = newSketch(context, id + "F12", { "sketchPlane" : qUnion([Q0])});
            skLineSegment(sketch, "E11.bottom", {"start": v(-188, 319.28) * mm, "end": v(-394, 319.28) * mm});
            skLineSegment(sketch, "E11.top", {"start": v(-188, -180.72) * mm, "end": v(-394, -180.72) * mm});
            skLineSegment(sketch, "E11.left", {"start": v(-188, 319.28) * mm, "end": v(-188, -180.72) * mm});
            skLineSegment(sketch, "E11.right", {"start": v(-394, 319.28) * mm, "end": v(-394, -180.72) * mm});
            skSolve(sketch);
        }
        {
            var Q0;
            Q0 = qSketchRegion(id + "F12", true);
            extrude(context, id + "F13", {"entities" : qUnion([Q0]), "depth" : 4 * mm, "offsetDistance" : 25 * mm});
        }
        {
            var Q0;
            Q0=makeQuery(id+"F3.opExtrude","CAP_FACE",FACE,{"disambiguationData":[OSD([sQuery(id+"F2.wireOp",EDGE,"E1.bottom"),sQuery(id+"F2.wireOp",EDGE,"E1.top"),sQuery(id+"F2.wireOp",EDGE,"E1.left"),sQuery(id+"F2.wireOp",EDGE,"E1.right")])],"isStart":false});
            var sketch = newSketch(context, id + "F14", { "sketchPlane" : qUnion([Q0])});
            skLineSegment(sketch, "E12.bottom", {"start": v(112.48, 170) * mm, "end": v(192.48, 170) * mm});
            skLineSegment(sketch, "E12.top", {"start": v(112.48, 0) * mm, "end": v(192.48, 0) * mm});
            skLineSegment(sketch, "E12.left", {"start": v(112.48, 170) * mm, "end": v(112.48, 0) * mm});
            skLineSegment(sketch, "E12.right", {"start": v(192.48, 170) * mm, "end": v(192.48, 0) * mm});
            skSolve(sketch);
        }
        {
            var Q0;
            Q0 = qSketchRegion(id + "F14", true);
            extrude(context, id + "F15", {"entities" : qUnion([Q0]), "depth" : 18 * mm, "offsetDistance" : 25 * mm});
        }
    });
